FCSTD DOCUMENT  (FreeCAD 0.20R29410 (Git))
Label: prancha-editavel-A4-modelo
License: All rights reserved
objects: Sketcher::SketchObject×1
note: 1 computed .brp shape members not serialized (recipe doc carries the construction recipe); baked Part::Feature solids carry a one-line shape summary decoded from their .brp

FEATURE [Sketcher::SketchObject] Sketch
  FullyConstrained = false
  sketch-geometry (11):
    g0: LineSegment StartX=-151.213 StartY=150 StartZ=0 EndX=145.787 EndY=150 EndZ=0
    g1: LineSegment StartX=145.787 StartY=150 StartZ=0 EndX=145.787 EndY=-60 EndZ=0
    g2: LineSegment StartX=145.787 StartY=-60 StartZ=0 EndX=-151.213 EndY=-60 EndZ=0
    g3: LineSegment StartX=-151.213 StartY=-60 StartZ=0 EndX=-151.213 EndY=150 EndZ=0
    g4: LineSegment StartX=-131.213 StartY=140 StartZ=0 EndX=135.787 EndY=140 EndZ=0
    g5: LineSegment StartX=135.787 StartY=140 StartZ=0 EndX=135.787 EndY=-50 EndZ=0
    g6: LineSegment StartX=135.787 StartY=-50 StartZ=0 EndX=-131.213 EndY=-50 EndZ=0
    g7: LineSegment StartX=-131.213 StartY=-50 StartZ=0 EndX=-131.213 EndY=140 EndZ=0
    g8: LineSegment StartX=135.531 StartY=-50 StartZ=0 EndX=-39.4693 EndY=-50 EndZ=0
    g9: LineSegment StartX=-39.4693 StartY=-50 StartZ=0 EndX=-39.4693 EndY=0 EndZ=0
    g10: LineSegment StartX=-39.4693 StartY=0 StartZ=0 EndX=135.531 EndY=0 EndZ=0
  constraints (22):
    c: Coincident(g0,g1)
    c: Coincident(g1,g2)
    c: Coincident(g2,g3)
    c: Coincident(g3,g0)
    c: Horizontal(g0)
    c: Horizontal(g2)
    c: Vertical(g1)
    c: Vertical(g3)
    c: Coincident(g4,g5)
    c: Coincident(g5,g6)
    c: Coincident(g6,g7)
    c: Coincident(g7,g4)
    c: Horizontal(g4)
    c: Vertical(g5)
    c: Vertical(g7)
    c: DistanceX(g0,g0) = 297
    c: DistanceY(g2,g0) = 210
    c: DistanceY(g4,g0) = 10
    c: DistanceX(g2,g6) = 20
    c: DistanceX(g4,g0) = 10
    c: DistanceY(g2,g6) = 10
    c: DistanceX(g10,g10) = 175
